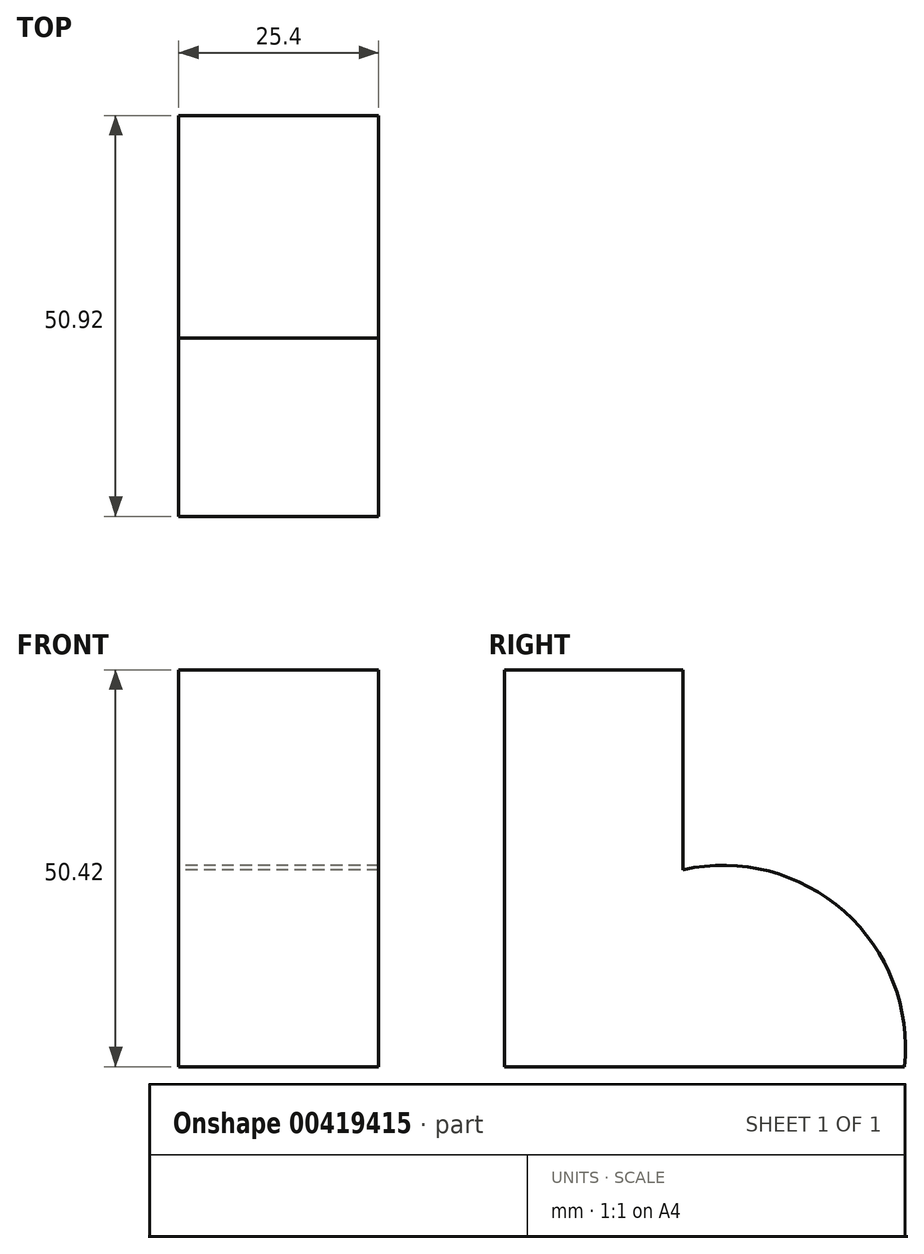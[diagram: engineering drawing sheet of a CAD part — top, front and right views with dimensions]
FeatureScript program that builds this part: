
annotation { "Feature Type Name" : "Feature", "Feature Type Description" : "" }
export const myFeature = defineFeature(function(context is Context, id is Id, definition is map)
    precondition{}
    {
        {
            var Q0;
            Q0=qCreatedBy(makeId("Right.planeOp"),FACE);
            var sketch = newSketch(context, id + "F0", { "sketchPlane" : qUnion([Q0])});
            skLineSegment(sketch, "E0", {"start": v(-22.67, 53.85) * mm, "end": v(-22.67, 3.05) * mm});
            skLineSegment(sketch, "E1", {"start": v(-22.67, 3.05) * mm, "end": v(28.13, 3.05) * mm});
            skLineSegment(sketch, "E2", {"start": v(-25.4, 53.47) * mm, "end": v(0, 53.47) * mm});
            skLineSegment(sketch, "E3", {"start": v(0, 53.47) * mm, "end": v(0, 28.07) * mm});
            skArc(sketch, "E4", {"start": v(28.13, 3.05) * mm, "mid": v(20.47, 22.76) * mm, "end": v(0, 28.07) * mm});
            skSolve(sketch);
        }
        {
            var Q0;
            Q0 = qSketchRegion(id + "F0", true);
            extrude(context, id + "F1", {"entities" : qUnion([Q0]), "depth" : 25.4 * mm});
        }
    });
